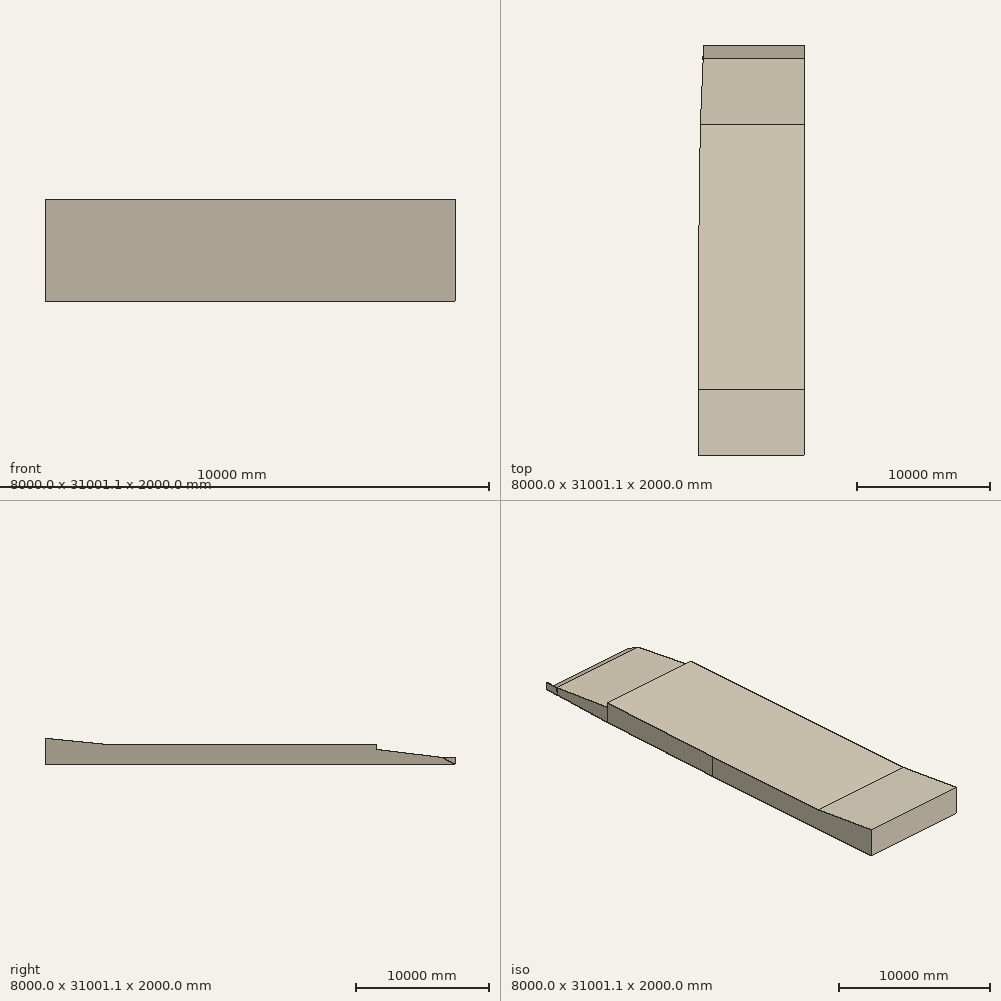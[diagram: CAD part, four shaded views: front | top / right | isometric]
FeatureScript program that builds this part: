
annotation { "Feature Type Name" : "Feature", "Feature Type Description" : "" }
export const myFeature = defineFeature(function(context is Context, id is Id, definition is map)
    precondition{}
    {
        {
            var Q0;
            Q0=qCreatedBy(makeId("Right.planeOp"),FACE);
            var sketch = newSketch(context, id + "F0", { "sketchPlane" : qUnion([Q0])});
            skLineSegment(sketch, "E0.top", {"start": v(0, -2000) * mm, "end": v(32000, -2000) * mm});
            skLineSegment(sketch, "E0.left", {"start": v(0, 0) * mm, "end": v(0, -2000) * mm});
            skLineSegment(sketch, "E1", {"start": v(0, 0) * mm, "end": v(5000, -500) * mm});
            skLineSegment(sketch, "E2", {"start": v(5000, -500) * mm, "end": v(25000, -500) * mm});
            skLineSegment(sketch, "E3", {"start": v(25000, -500) * mm, "end": v(25000, -840) * mm});
            skLineSegment(sketch, "E4", {"start": v(25000, -840) * mm, "end": v(30000, -1450) * mm});
            skLineSegment(sketch, "E5", {"start": v(30000, -1450) * mm, "end": v(31000, -2000) * mm});
            skSolve(sketch);
        }
        {
            var Q0;
            {var subQ0=sQuery(id+"F0.wireOp",EDGE,"E0.left");Q0=makeQuery(id+"F0.imprint","IMPRINT",FACE,{"disambiguationData":[TD([[makeQuery(id+"F0.imprint","IMPRINT",EDGE,{"derivedFrom":subQ0}),1.0]])]});}
            extrude(context, id + "F1", {"entities" : qUnion([Q0]), "depth" : -8000 * mm, "offsetDistance" : 25 * mm});
        }
        {
            var Q0;
            Q0=makeQuery(id+"F1.opExtrude","CAP_FACE",FACE,{"disambiguationData":[OSD([sQuery(id+"F0.wireOp",EDGE,"E0.top"),sQuery(id+"F0.wireOp",EDGE,"E0.left"),sQuery(id+"F0.wireOp",EDGE,"E1"),sQuery(id+"F0.wireOp",EDGE,"E2"),sQuery(id+"F0.wireOp",EDGE,"E3"),sQuery(id+"F0.wireOp",EDGE,"E4"),sQuery(id+"F0.wireOp",EDGE,"E5")])],"isStart":false});
            var sketch = newSketch(context, id + "F2", { "sketchPlane" : qUnion([Q0])});
            skLineSegment(sketch, "E6.bottom", {"start": v(-5000, -500) * mm, "end": v(-15000, -500) * mm});
            skLineSegment(sketch, "E6.top", {"start": v(-5000, 5500) * mm, "end": v(-15000, 5500) * mm});
            skLineSegment(sketch, "E6.left", {"start": v(-5000, -500) * mm, "end": v(-5000, 5500) * mm});
            skLineSegment(sketch, "E6.right", {"start": v(-15000, -500) * mm, "end": v(-15000, 5500) * mm});
            skSolve(sketch);
        }
        {
            var Q0;
            Q0=makeQuery(id+"FXcwu4goBAmFRLV_1.opExtrude","SWEPT_FACE",FACE,{"disambiguationData":[OSD([sQuery(id+"F2.wireOp",EDGE,"E6.right")])]});
            var sketch = newSketch(context, id + "F3", { "sketchPlane" : qUnion([Q0])});
            skLineSegment(sketch, "E7", {"start": v(5250, 5500) * mm, "end": v(8500, 5500) * mm});
            skLineSegment(sketch, "E8", {"start": v(8500, 5500) * mm, "end": v(5250, 7000) * mm});
            skLineSegment(sketch, "E9", {"start": v(5250, 7000) * mm, "end": v(5250, 5500) * mm, "construction": true});
            skLineSegment(sketch, "E10.MirrorCS", {"start": v(2000, 5500) * mm, "end": v(5250, 7000) * mm});
            skLineSegment(sketch, "E11.MirrorCS", {"start": v(5250, 5500) * mm, "end": v(2000, 5500) * mm});
            skSolve(sketch);
        }
        {
            var Q0;
            Q0=makeQuery(id+"F1.opExtrude","SWEPT_FACE",FACE,{"disambiguationData":[OSD([sQuery(id+"F0.wireOp",EDGE,"E2")])]});
            var sketch = newSketch(context, id + "F4", { "sketchPlane" : qUnion([Q0])});
            skLineSegment(sketch, "E12.bottom", {"start": v(0, 25000) * mm, "end": v(-2670, 25000) * mm});
            skLineSegment(sketch, "E12.top", {"start": v(0, 18000) * mm, "end": v(-2670, 18000) * mm});
            skLineSegment(sketch, "E12.left", {"start": v(0, 25000) * mm, "end": v(0, 18000) * mm});
            skLineSegment(sketch, "E12.right", {"start": v(-2670, 25000) * mm, "end": v(-2670, 18000) * mm});
            skSolve(sketch);
        }
        {
            var Q0;
            Q0=makeQuery(id+"F1.opExtrude","SWEPT_FACE",FACE,{"disambiguationData":[OSD([sQuery(id+"F0.wireOp",EDGE,"E2")])]});
            var sketch = newSketch(context, id + "F5", { "sketchPlane" : qUnion([Q0])});
            skLineSegment(sketch, "E13", {"start": v(-8000, 15000) * mm, "end": v(-13098.88, 15000) * mm});
            skLineSegment(sketch, "E14", {"start": v(-13098.88, 15000) * mm, "end": v(-13098.88, 34500) * mm});
            skLineSegment(sketch, "E15", {"start": v(-13098.88, 34500) * mm, "end": v(-7454.03, 34500) * mm});
            skLineSegment(sketch, "E16", {"start": v(-7454.03, 34500) * mm, "end": v(-7870, 25000) * mm});
            skLineSegment(sketch, "E17", {"start": v(-7870, 25000) * mm, "end": v(-8000, 15000) * mm});
            skSolve(sketch);
        }
        {
            var Q0;
            Q0=makeQuery(id+"F5.imprint","IMPRINT",FACE,{"disambiguationData":[TD([[makeQuery(id+"F5.imprint","IMPRINT",EDGE,{"derivedFrom":sQuery(id+"F5.wireOp",EDGE,"E13")}),-1.0]])]});
            var Q1;
            {var subQ0=sQuery(id+"F5.wireOp",EDGE,"E17");Q1=makeQuery(id+"F5.imprint","IMPRINT",FACE,{"disambiguationData":[TD([[makeQuery(id+"F5.imprint","IMPRINT",EDGE,{"derivedFrom":subQ0}),-1.0]])]});}
            var Q2;
            Q2=makeQuery(id+"F1.opExtrude","SWEPT_FACE",FACE,{"disambiguationData":[OSD([sQuery(id+"F0.wireOp",EDGE,"E0.top")])]});
            extrude(context, id + "F6", {"entities" : qUnion([Q0, Q1]), "operationType" : NewBodyOperationType.REMOVE, "endBound" : BoundingType.UP_TO_SURFACE, "oppositeDirection" : true, "depth" : 25 * mm, "endBoundEntityFace" : qUnion([Q2]), "offsetDistance" : 25 * mm});
        }
        {
            var Q0;
            Q0=makeQuery(id+"F6.boolean.opBoolean","COPY",FACE,{"derivedFrom":makeQuery(id+"F6.opExtrude","SWEPT_FACE",FACE,{"disambiguationData":[OSD([sQuery(id+"F5.wireOp",EDGE,"E16")])]})});
            var sketch = newSketch(context, id + "F7", { "sketchPlane" : qUnion([Q0])});
            skLineSegment(sketch, "E18.bottom", {"start": v(-30637.55, -2000) * mm, "end": v(-30637.55, -2000) * mm});
            skLineSegment(sketch, "E19", {"start": v(-30637.55, -2000) * mm, "end": v(-30637.55, -1450) * mm});
            skLineSegment(sketch, "E20", {"start": v(-30637.55, -1450) * mm, "end": v(-29636.6, -1450) * mm});
            skLineSegment(sketch, "E21", {"start": v(-29636.6, -1450) * mm, "end": v(-29569.56, -2000) * mm});
            skLineSegment(sketch, "E22", {"start": v(-29569.56, -2000) * mm, "end": v(-30637.55, -2000) * mm});
            skSolve(sketch);
        }
        {
            var Q0;
            Q0=makeQuery(id+"F7.imprint","IMPRINT",FACE,{"disambiguationData":[TD([[makeQuery(id+"F7.imprint","IMPRINT",EDGE,{"derivedFrom":sQuery(id+"F7.wireOp",EDGE,"E19")}),-1.0]])]});
            var Q1;
            Q1=makeQuery(id+"F7.imprint","IMPRINT",FACE,{"disambiguationData":[TD([[makeQuery(id+"F7.imprint","IMPRINT",EDGE,{"derivedFrom":sQuery(id+"F7.wireOp",EDGE,"E21")}),-1.0]])]});
            extrude(context, id + "F8", {"entities" : qUnion([Q0, Q1]), "operationType" : NewBodyOperationType.ADD, "depth" : 25 * mm, "offsetDistance" : 25 * mm});
        }
    });
